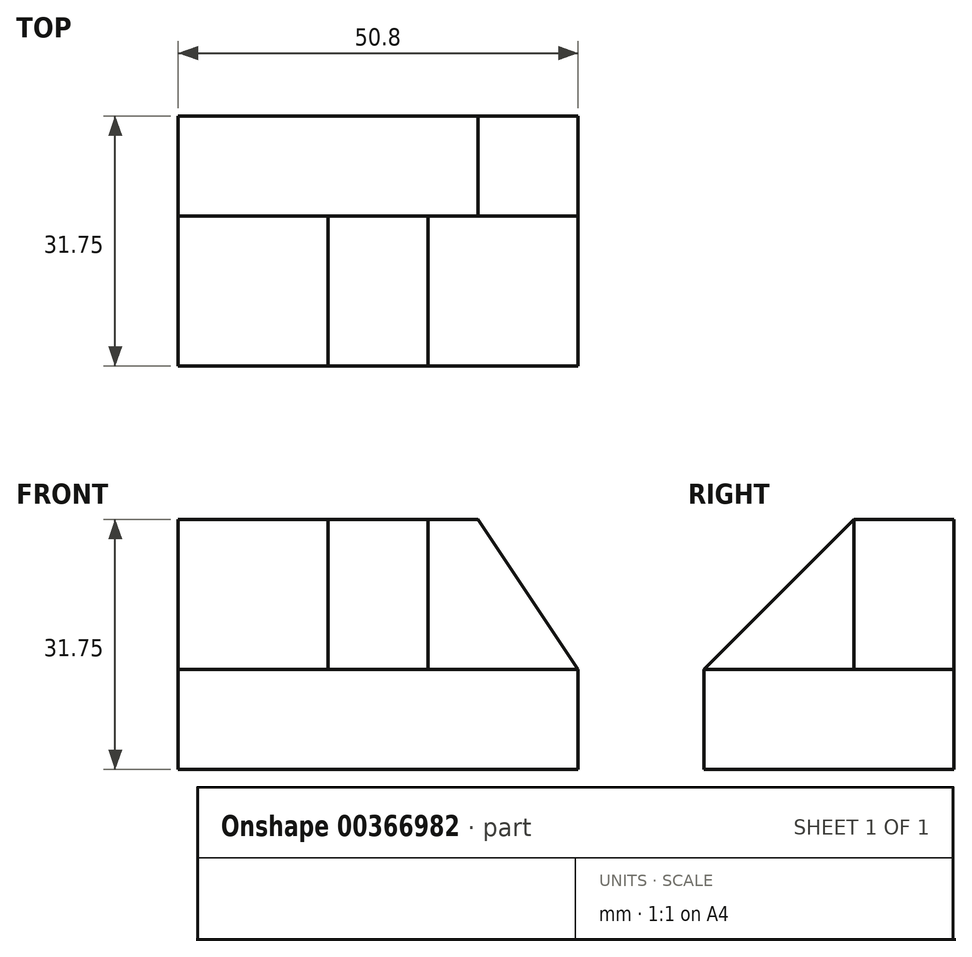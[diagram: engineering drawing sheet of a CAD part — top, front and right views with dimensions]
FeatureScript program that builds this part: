
annotation { "Feature Type Name" : "Feature", "Feature Type Description" : "" }
export const myFeature = defineFeature(function(context is Context, id is Id, definition is map)
    precondition{}
    {
        {
            var Q0;
            Q0=qCreatedBy(makeId("Front.planeOp"),FACE);
            var sketch = newSketch(context, id + "F0", { "sketchPlane" : qUnion([Q0])});
            skLineSegment(sketch, "E0", {"start": v(0, 0) * mm, "end": v(50.8, 0) * mm});
            skLineSegment(sketch, "E1", {"start": v(50.8, 0) * mm, "end": v(50.8, 31.75) * mm});
            skLineSegment(sketch, "E2", {"start": v(50.8, 31.75) * mm, "end": v(0, 31.75) * mm});
            skLineSegment(sketch, "E3", {"start": v(0, 31.75) * mm, "end": v(0, 0) * mm});
            skSolve(sketch);
        }
        {
            var Q0;
            Q0=makeQuery(id+"F0.imprint","IMPRINT",FACE,{"disambiguationData":[TD([[makeQuery(id+"F0.imprint","IMPRINT",EDGE,{"derivedFrom":sQuery(id+"F0.wireOp",EDGE,"E0")}),1.0]])]});
            extrude(context, id + "F1", {"entities" : qUnion([Q0]), "depth" : 31.75 * mm});
        }
        {
            var Q0;
            Q0=makeQuery(id+"F1.opExtrude","CAP_FACE",FACE,{"disambiguationData":[OSD([sQuery(id+"F0.wireOp",EDGE,"E0"),sQuery(id+"F0.wireOp",EDGE,"E1"),sQuery(id+"F0.wireOp",EDGE,"E2"),sQuery(id+"F0.wireOp",EDGE,"E3")])],"isStart":false});
            var sketch = newSketch(context, id + "F2", { "sketchPlane" : qUnion([Q0])});
            skLineSegment(sketch, "E4", {"start": v(31.75, 31.75) * mm, "end": v(31.75, 12.7) * mm});
            skLineSegment(sketch, "E5", {"start": v(31.75, 12.7) * mm, "end": v(50.8, 12.7) * mm});
            skSolve(sketch);
        }
        {
            var Q0;
            {var subQ0=sQuery(id+"F2.wireOp",EDGE,"E4");Q0=makeQuery(id+"F2.imprint","IMPRINT",FACE,{"disambiguationData":[TD([[makeQuery(id+"F2.imprint","IMPRINT",EDGE,{"derivedFrom":subQ0}),1.0]])]});}
            extrude(context, id + "F3", {"entities" : qUnion([Q0]), "operationType" : NewBodyOperationType.REMOVE, "oppositeDirection" : true, "depth" : 19.05 * mm});
        }
        {
            var Q0;
            Q0=makeQuery(id+"F3.boolean.opBoolean","COPY",FACE,{"derivedFrom":makeQuery(id+"F3.opExtrude","CAP_FACE",FACE,{"disambiguationData":[OSD([sQuery(id+"F0.wireOp",EDGE,"E1"),sQuery(id+"F0.wireOp",EDGE,"E2"),sQuery(id+"F2.wireOp",EDGE,"E4"),sQuery(id+"F2.wireOp",EDGE,"E5")])],"isStart":false})});
            var sketch = newSketch(context, id + "F4", { "sketchPlane" : qUnion([Q0])});
            skLineSegment(sketch, "E6", {"start": v(38.1, 31.75) * mm, "end": v(50.8, 12.7) * mm});
            skSolve(sketch);
        }
        {
            var Q0;
            {var subQ0=sQuery(id+"F4.wireOp",EDGE,"E6");Q0=makeQuery(id+"F4.imprint","IMPRINT",FACE,{"disambiguationData":[TD([[makeQuery(id+"F4.imprint","IMPRINT",EDGE,{"derivedFrom":subQ0}),1.0]])]});}
            extrude(context, id + "F5", {"entities" : qUnion([Q0]), "operationType" : NewBodyOperationType.REMOVE, "oppositeDirection" : true, "depth" : 12.7 * mm});
        }
        {
            var Q0;
            Q0=makeQuery(id+"F3.boolean.opBoolean","COPY",FACE,{"derivedFrom":makeQuery(id+"F3.opExtrude","SWEPT_FACE",FACE,{"disambiguationData":[OSD([sQuery(id+"F2.wireOp",EDGE,"E4")])]})});
            var sketch = newSketch(context, id + "F6", { "sketchPlane" : qUnion([Q0])});
            skLineSegment(sketch, "E7", {"start": v(-12.7, 31.75) * mm, "end": v(-31.75, 12.7) * mm});
            skSolve(sketch);
        }
        {
            var Q0;
            Q0=makeQuery(id+"F6.imprint","IMPRINT",FACE,{"disambiguationData":[TD([[makeQuery(id+"F6.imprint","IMPRINT",EDGE,{"derivedFrom":sQuery(id+"F6.wireOp",EDGE,"E7")}),-1.0]])]});
            extrude(context, id + "F7", {"entities" : qUnion([Q0]), "operationType" : NewBodyOperationType.REMOVE, "oppositeDirection" : true, "depth" : 12.7 * mm});
        }
        {
            var Q0;
            Q0=makeQuery(id+"F1.opExtrude","SWEPT_FACE",FACE,{"disambiguationData":[OSD([sQuery(id+"F0.wireOp",EDGE,"E3")])]});
            var sketch = newSketch(context, id + "F8", { "sketchPlane" : qUnion([Q0])});
            skLineSegment(sketch, "E8", {"start": v(12.7, 31.75) * mm, "end": v(12.7, 12.7) * mm});
            skLineSegment(sketch, "E9", {"start": v(12.7, 12.7) * mm, "end": v(31.75, 12.7) * mm});
            skSolve(sketch);
        }
        {
            var Q0;
            {var subQ0=sQuery(id+"F8.wireOp",EDGE,"E8");Q0=makeQuery(id+"F8.imprint","IMPRINT",FACE,{"disambiguationData":[TD([[makeQuery(id+"F8.imprint","IMPRINT",EDGE,{"derivedFrom":subQ0}),1.0]])]});}
            extrude(context, id + "F9", {"entities" : qUnion([Q0]), "operationType" : NewBodyOperationType.REMOVE, "oppositeDirection" : true, "depth" : 19.05 * mm});
        }
    });
